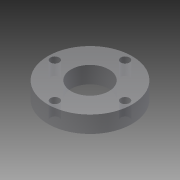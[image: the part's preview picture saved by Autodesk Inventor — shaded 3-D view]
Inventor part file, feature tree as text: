
AUTODESK INVENTOR PART (.ipt)
format: ipt  version: 2013 (Build 170138000, 138)  size: 92,160 bytes
history: native  units: in
note: dims shown in document units (in); Inventor stores cm internally (conversion verified against a paired STEP export)
features: extrude x1, sketch x1
ambient origin geometry x8: Origin, YZ Plane, XZ Plane, XY Plane, X Axis, Y Axis, Z Axis, Center Point
bodies: Solid1 (feature_tree)
feature tree (2):
  extrude  "Extrusion1"  Depth=2.09in
  sketch  "Sketch1"  dims[d0=1.125in d1=2.09in d2=2.5in d3=0.26in d4=0.26in d5=0.26in d6=0.26in d7=0.5in d8=0.0in]
